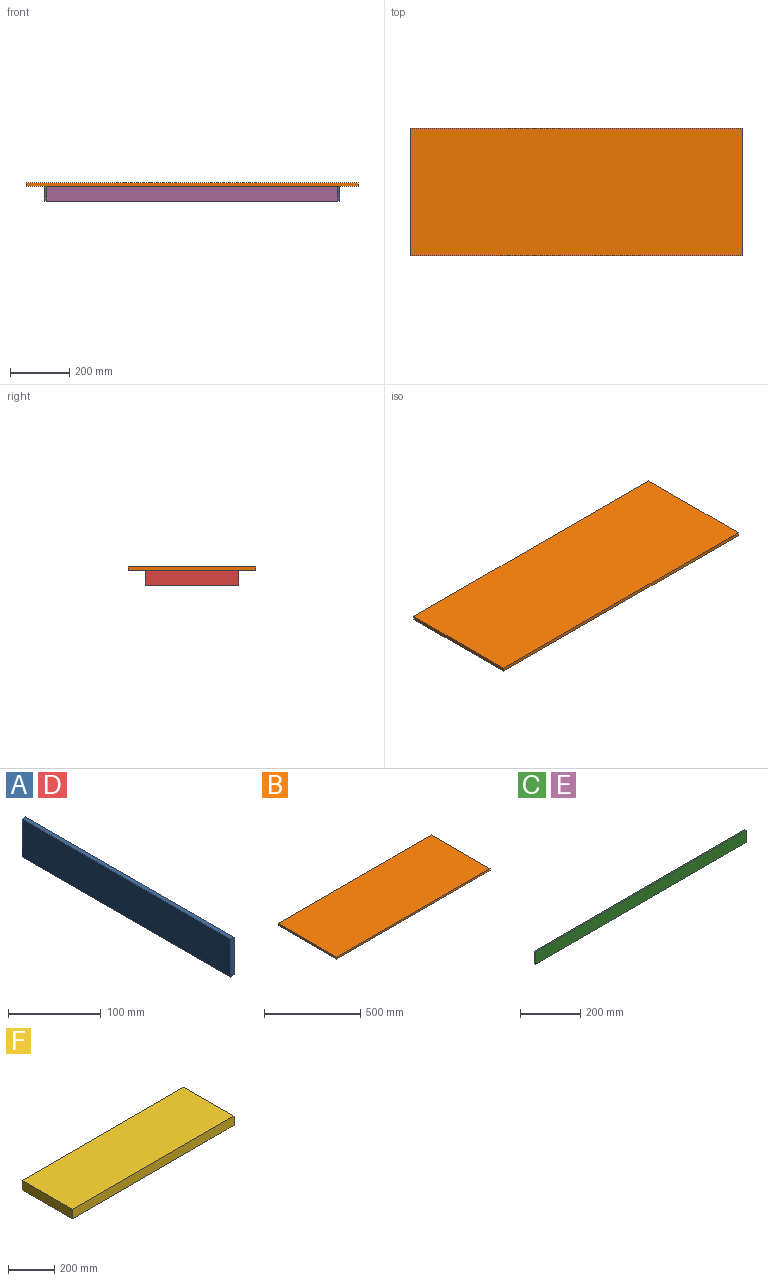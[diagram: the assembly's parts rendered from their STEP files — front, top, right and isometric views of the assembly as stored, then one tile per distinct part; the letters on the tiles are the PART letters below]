
ASSEMBLY  parts=6 mates=5
PART A: 6 faces, bbox 6x318x50 mm
  f0: plane 50x6mm, normal (0,1,0), area 300mm2, adj f1,f3,f4,f5
  f1: plane 318x6mm, normal (0,0,1), area 1908mm2, adj f0,f2,f4,f5
  f2: plane 50x6mm, normal (0,-1,0), area 300mm2, adj f1,f3,f4,f5
  f3: plane 318x6mm, normal (0,0,-1), area 1908mm2, adj f0,f2,f4,f5
  f4: plane 318x50mm, normal (1,0,0), area 15900mm2, adj f0,f1,f2,f3
  f5: plane 318x50mm, normal (-1,0,0), area 15900mm2, adj f0,f1,f2,f3
PART B: 6 faces, bbox 1124x430x12 mm
  f0: plane 1124x12mm, normal (0,-1,0), area 13488mm2, adj f1,f3,f4,f5
  f1: plane 430x12mm, normal (1,0,0), area 5160mm2, adj f0,f2,f4,f5
  f2: plane 1124x12mm, normal (0,1,0), area 13488mm2, adj f1,f3,f4,f5
  f3: plane 430x12mm, normal (-1,0,0), area 5160mm2, adj f0,f2,f4,f5
  f4: plane 1124x430mm, normal (0,0,1), area 483320mm2, adj f0,f1,f2,f3
  f5: plane 1124x430mm, normal (0,0,-1), area 483320mm2, adj f0,f1,f2,f3
PART C: 6 faces, bbox 988x6x50 mm
  f0: plane 50x6mm, normal (1,0,0), area 300mm2, adj f1,f3,f4,f5
  f1: plane 988x6mm, normal (0,0,1), area 5928mm2, adj f0,f2,f4,f5
  f2: plane 50x6mm, normal (-1,0,0), area 300mm2, adj f1,f3,f4,f5
  f3: plane 988x6mm, normal (0,0,-1), area 5928mm2, adj f0,f2,f4,f5
  f4: plane 988x50mm, normal (0,-1,0), area 49400mm2, adj f0,f1,f2,f3
  f5: plane 988x50mm, normal (0,1,0), area 49400mm2, adj f0,f1,f2,f3
PART D: same geometry as A
PART E: same geometry as C
PART F: 6 faces, bbox 988x306x50 mm
  f0: plane 306x50mm, normal (1,0,0), area 15300mm2, adj f1,f3,f4,f5
  f1: plane 988x50mm, normal (0,1,0), area 49400mm2, adj f0,f2,f4,f5
  f2: plane 306x50mm, normal (-1,0,0), area 15300mm2, adj f1,f3,f4,f5
  f3: plane 988x50mm, normal (0,-1,0), area 49400mm2, adj f0,f2,f4,f5
  f4: plane 988x306mm, normal (0,0,1), area 302328mm2, adj f0,f1,f2,f3
  f5: plane 988x306mm, normal (0,0,-1), area 302328mm2, adj f0,f1,f2,f3
PLACE A t=(280.51,129.33,86.68)mm
PLACE B t=(-213.49,129.33,111.68)mm
PLACE C t=(-213.49,288.33,86.68)mm
PLACE D t=(-713.49,129.33,86.68)mm
PLACE E t=(-213.49,-23.67,86.68)mm
PLACE F t=(-213.49,129.33,61.68)mm
MATE fastened D.f4 <-> E.f2  axis (1,0,0) through (-707.49,-29.67,111.68)mm
MATE fastened F.f5 <-> E.f3  axis (0,0,-1) through (280.51,-23.67,61.68)mm
MATE fastened A.f5 <-> E.f0  axis (-1,0,0) through (280.51,-29.67,111.68)mm
MATE fastened B.f5 <-> F.f4  axis (0,0,-1) through (-213.49,129.33,111.68)mm
MATE fastened C.f0 <-> A.f5  axis (1,0,0) through (280.51,288.33,111.68)mm
